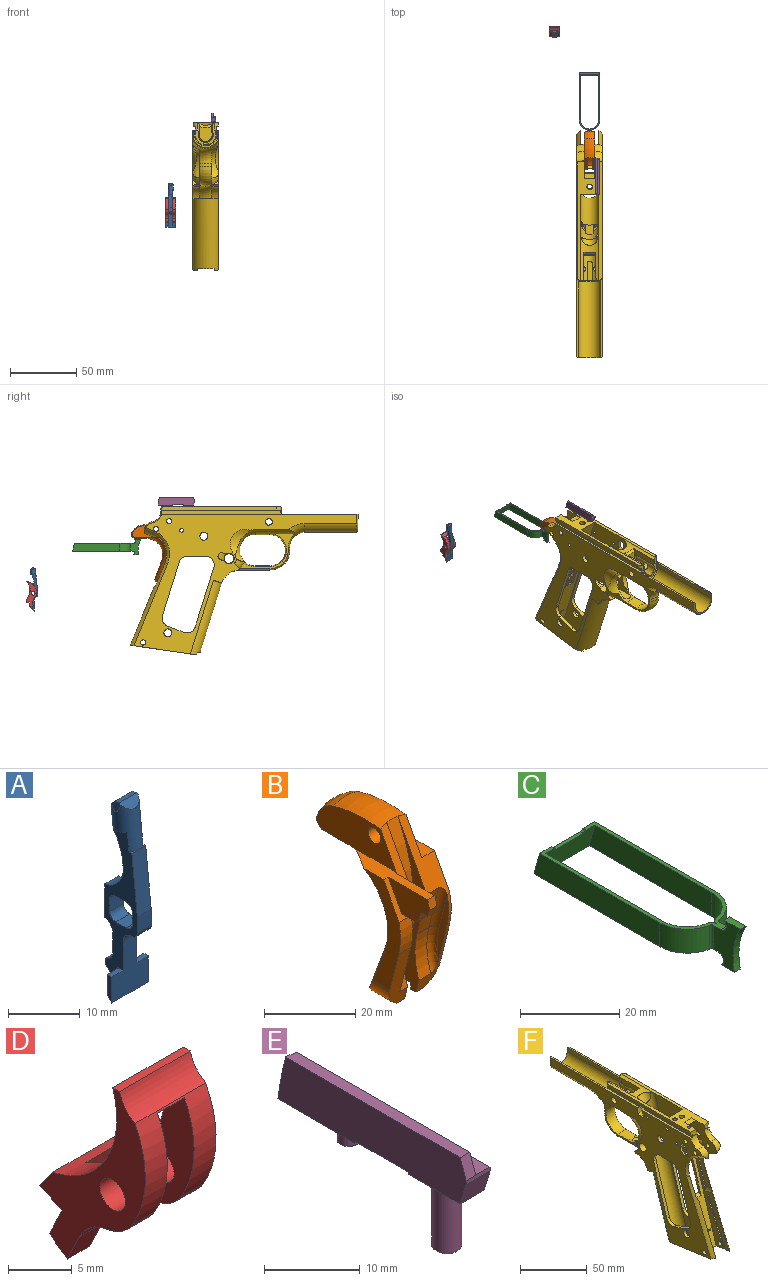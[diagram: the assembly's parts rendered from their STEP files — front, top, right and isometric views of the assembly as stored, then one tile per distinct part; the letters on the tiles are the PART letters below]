
ASSEMBLY  parts=6 mates=3
PART A: 42 faces, bbox 7.3x6.5x33 mm
  f0: cylinder r=1.97mm len=8.04mm, axis (0,0.1,0.99), area 53.4mm2, adj f2,f3,f5,f6,f7,f34,f35,f36
  f1: plane 3.38x0.76mm, normal (0,0.1,0.99), area 2.6mm2, adj f2,f3,f40,f41
  f2: plane 3.61x1.97mm, normal (0,0.77,0.64), area 7.5mm2, adj f0,f1,f40,f41
  f3: plane 3.47x1.44mm, normal (0,-0.59,0.81), area 4.8mm2, adj f0,f1,f40,f41
  f4: plane 10.31x2.72mm, normal (0,-0.99,0.1), area 28.2mm2, adj f5,f7,f15,f34,f35
  f5: plane 27.19x6.4mm, normal (-1,0,0), area 69.5mm2, adj f0,f4,f6,f8,f9,f10,f11,f12
  f6: cylinder r=9.92mm len=6.65mm, axis (-1,0,0), area 19mm2, adj f0,f5,f7,f26
  f7: plane 27.19x6.4mm, normal (1,0,0), area 69.5mm2, adj f0,f4,f6,f8,f9,f10,f11,f12
  f8: cylinder r=1.19mm len=2.72mm, axis (-1,0,0), area 5.1mm2, adj f5,f7,f9,f27
  f9: plane 2.72x2.04mm, normal (0,-1,0), area 5.5mm2, adj f5,f7,f8,f10
  f10: cylinder r=1.19mm len=2.72mm, axis (-1,0,0), area 5.1mm2, adj f5,f7,f9,f11
  f11: plane 2.72x2.04mm, normal (0,0,1), area 5.5mm2, adj f5,f7,f10,f12
  f12: cylinder r=1.19mm len=2.72mm, axis (-1,0,0), area 5.1mm2, adj f5,f7,f11,f13
  f13: plane 2.72x2.04mm, normal (0,1,0), area 5.5mm2, adj f5,f7,f12,f14
  f14: cylinder r=1.19mm len=2.72mm, axis (-1,0,0), area 5.1mm2, adj f5,f7,f13,f27
  f15: plane 2.72x2.65mm, normal (0,-1,0), area 7.2mm2, adj f4,f5,f7,f16
  f16: cylinder r=1.19mm len=2.72mm, axis (-1,0,0), area 5.1mm2, adj f5,f7,f15,f17
  f17: plane 2.72x0.02mm, normal (0,0,-1), area 0mm2, adj f5,f7,f16,f18
  f18: cylinder r=1.59mm len=2.72mm, axis (-1,0,0), area 6.8mm2, adj f5,f7,f17,f19
  f19: plane 9.44x7.24mm, normal (0,-1,0), area 45.5mm2, adj f5,f7,f18,f20,f29,f31,f32,f33
  f20: plane 7.3x3.95mm, normal (0,0.74,-0.67), area 20.3mm2, adj f5,f7,f19,f21,f28,f30,f32,f33
  f21: plane 2.72x0.79mm, normal (0,1,0), area 2.2mm2, adj f5,f7,f20,f22
  f22: cylinder r=1.98mm len=2.72mm, axis (-1,0,0), area 7.1mm2, adj f5,f7,f21,f23
  f23: plane 3.04x2.72mm, normal (0,1,0), area 8.3mm2, adj f5,f7,f22,f24
  f24: cylinder r=1.98mm len=2.72mm, axis (-1,0,0), area 7.4mm2, adj f5,f7,f23,f25
  f25: plane 5.74x2.72mm, normal (0,1,0), area 15.6mm2, adj f5,f7,f24,f26
  f26: cylinder r=4.37mm len=4.31mm, axis (-1,0,0), area 16.6mm2, adj f5,f6,f7,f25
  f27: plane 2.72x2.04mm, normal (0,0,-1), area 5.5mm2, adj f5,f7,f8,f14
  f28: plane 3.41x2.13mm, normal (0,1,0), area 7.3mm2, adj f20,f29,f33,f38
  f29: plane 2.26x1.02mm, normal (0,0,1), area 2mm2, adj f5,f19,f28,f33,f38
  f30: plane 3.41x2.13mm, normal (0,1,0), area 7.3mm2, adj f20,f31,f32,f39
  f31: plane 2.26x1.02mm, normal (0,0,1), area 2mm2, adj f7,f19,f30,f32,f39
  f32: plane 4.39x0.89mm, normal (1,0,0), area 3.5mm2, adj f19,f20,f30,f31
  f33: plane 4.39x0.89mm, normal (-1,0,0), area 3.5mm2, adj f19,f20,f28,f29
  f34: plane 1.36x0.54mm, normal (0,0.1,0.99), area 0.2mm2, adj f0,f4,f7
  f35: plane 1.36x0.54mm, normal (0,0.1,0.99), area 0.2mm2, adj f0,f4,f5
  f36: plane 2.83x0.61mm, normal (0,-0.1,-0.99), area 1.2mm2, adj f0,f7
  f37: plane 2.83x0.61mm, normal (0,-0.1,-0.99), area 1.2mm2, adj f0,f5
  f38: cylinder r=0.13mm len=3.41mm, axis (0,0,-1), area 0.7mm2, adj f5,f20,f28,f29
  f39: cylinder r=0.13mm len=3.41mm, axis (0,0,1), area 0.7mm2, adj f7,f20,f30,f31
  f40: plane 1.67x1.65mm, normal (-0.98,0.02,0.17), area 1.9mm2, adj f0,f1,f2,f3
  f41: plane 1.67x1.65mm, normal (0.98,0.02,0.17), area 1.9mm2, adj f0,f1,f2,f3
PART B: 46 faces, bbox 16.9x38.1x47.9 mm
  f0: plane 18.69x9.94mm, normal (0,-0.88,0.47), area 60.9mm2, adj f2,f3,f9,f13,f15,f17,f20,f32
  f1: plane 17.05x6.12mm, normal (0,-0.97,-0.24), area 68.5mm2, adj f2,f3,f5,f9,f37,f41,f43
  f2: cylinder r=19.05mm len=8.65mm, axis (-1,0,0), area 33mm2, adj f0,f1,f9,f43
  f3: plane 44.48x8.86mm, normal (1,0,0), area 92.1mm2, adj f0,f1,f5,f6,f7,f13,f35,f41
  f4: plane 44.47x8.86mm, normal (-1,0,0), area 92.1mm2, adj f6,f10,f13,f14,f27,f28,f35,f38
  f5: plane 2.42x1.64mm, normal (0,-0.06,-1), area 3.7mm2, adj f1,f3,f7,f37
  f6: plane 12.62x5.63mm, normal (0,-0.06,-1), area 51.1mm2, adj f3,f4,f7,f12,f28,f35,f36,f37
  f7: plane 4.57x1.82mm, normal (0,1,-0.06), area 6.4mm2, adj f3,f5,f6,f37
  f8: plane 28.65x11.28mm, normal (1,0,0), area 121mm2, adj f10,f11,f14,f21,f26,f30,f36
  f9: plane 28.65x11.28mm, normal (-1,0,0), area 121mm2, adj f0,f1,f2,f11,f17,f30,f37
  f10: plane 17.05x6.1mm, normal (0,-0.97,-0.24), area 28mm2, adj f4,f8,f26,f27,f36,f39,f40,f44
  f11: cylinder r=11.91mm len=15.72mm, axis (0,0.34,-0.94), area 252.7mm2, adj f8,f9,f12,f30,f36,f37
  f12: extruded ~14.05x3.13mm, area 20.3mm2, adj f6,f11,f36,f37
  f13: torus R=23.81mm, axis (-1,0,0), area 117.5mm2, adj f0,f3,f4,f14,f15,f16,f34,f35
  f14: plane 18.69x9.94mm, normal (0,-0.88,0.47), area 73.8mm2, adj f4,f8,f13,f16,f21,f26,f38,f45
  f15: plane 24.62x9.44mm, normal (-1,0,0), area 173.6mm2, adj f0,f13,f17,f25,f29,f30,f31,f34
  f16: plane 24.62x9.44mm, normal (1,0,0), area 173.6mm2, adj f13,f14,f21,f25,f29,f30,f31,f34
  f17: plane 25.36x3.94mm, normal (0,0,1), area 63.6mm2, adj f0,f9,f15,f18,f30,f32,f33
  f18: plane 2.57x2.21mm, normal (0,-0.98,0.21), area 5.8mm2, adj f17,f19,f32,f33
  f19: plane 2.21x1.82mm, normal (0,-0.95,-0.31), area 4.2mm2, adj f18,f24,f32,f33
  f20: plane 3.84x2.21mm, normal (0,0,-1), area 8.5mm2, adj f0,f23,f32,f33
  f21: plane 13.16x3.94mm, normal (0,0,1), area 36.6mm2, adj f8,f14,f16,f30
  f22: plane 2.26x2.21mm, normal (0,-0.95,-0.31), area 5.2mm2, adj f23,f24,f32,f33
  f23: cylinder r=1.59mm len=2.21mm, axis (-1,0,0), area 4.4mm2, adj f20,f22,f32,f33
  f24: plane 2.21x1.98mm, normal (0,0,-1), area 4.4mm2, adj f19,f22,f32,f33
  f25: cylinder r=11.91mm len=8.18mm, axis (0,-1,0), area 65.4mm2, adj f15,f16,f30,f31
  f26: cylinder r=19.05mm len=8.65mm, axis (-1,0,0), area 7.1mm2, adj f8,f10,f14,f40,f45
  f27: plane 2.39x1.64mm, normal (0,-0.06,-1), area 3.7mm2, adj f4,f10,f28,f36
  f28: plane 4.54x1.82mm, normal (0,1,-0.06), area 6.4mm2, adj f4,f6,f27,f36
  f29: cylinder r=1.98mm len=7.85mm, axis (-1,0,0), area 97.7mm2, adj f15,f16
  f30: torus R=24.61mm, axis (1,0,0), area 403.8mm2, adj f8,f9,f11,f15,f16,f17,f21,f25
  f31: revolved ~7.85x3.38mm, area 36.6mm2, adj f15,f16,f25,f34
  f32: plane 12.77x7.75mm, normal (1,0,0), area 71mm2, adj f0,f17,f18,f19,f20,f22,f23,f24
  f33: plane 12.77x7.75mm, normal (-1,0,0), area 71mm2, adj f0,f17,f18,f19,f20,f22,f23,f24
  f34: revolved ~7.85x6.03mm, area 65.7mm2, adj f13,f15,f16,f31
  f35: cylinder r=51.07mm len=42.99mm, axis (1,0,0), area 155.4mm2, adj f3,f4,f6,f13
  f36: cylinder r=6.75mm len=7.07mm, axis (0,1,0), area 32.8mm2, adj f6,f8,f10,f11,f12,f27,f28
  f37: cylinder r=6.75mm len=7.07mm, axis (0,1,0), area 32.8mm2, adj f1,f5,f6,f7,f9,f11,f12
  f38: plane 12.16x3.7mm, normal (0,-0.97,-0.24), area 46.3mm2, adj f4,f14,f39,f45
  f39: cylinder r=20.64mm len=12.01mm, axis (-1,0,0), area 45.1mm2, adj f4,f10,f38,f44
  f40: plane 18.96x3.57mm, normal (-1,0,0), area 26.1mm2, adj f10,f26,f44,f45
  f41: cylinder r=20.64mm len=12.01mm, axis (-1,0,0), area 28.5mm2, adj f1,f3,f42,f43
  f42: plane 12.16x3.03mm, normal (0,-0.97,-0.24), area 29.3mm2, adj f0,f3,f41,f43
  f43: plane 24.18x5.16mm, normal (1,0,0), area 61.2mm2, adj f0,f1,f2,f41,f42
  f44: torus R=19.05mm, axis (1,0,0), area 27.3mm2, adj f10,f39,f40,f45
  f45: cylinder r=1.59mm len=12.55mm, axis (0,-0.24,0.97), area 29.7mm2, adj f14,f26,f38,f40,f44
PART C: 26 faces, bbox 15.7x51.8x11.4 mm
  f0: plane 44.64x15.7mm, normal (0,0,1), area 85mm2, adj f2,f3,f4,f5,f6,f7,f8,f9
  f1: plane 45.47x15.7mm, normal (0,0,-1), area 94.3mm2, adj f2,f3,f4,f5,f6,f7,f8,f9
  f2: plane 35.87x5.89mm, normal (-1,0,0), area 206.6mm2, adj f0,f1,f8,f16
  f3: plane 35x5.89mm, normal (-1,0,0), area 201.5mm2, adj f0,f1,f7,f17
  f4: cylinder r=1.47mm len=5.89mm, axis (0,0,-1), area 12.1mm2, adj f0,f1,f5,f15
  f5: cylinder r=7.01mm len=6.9mm, axis (0,0,-1), area 57.7mm2, adj f0,f1,f4,f6
  f6: plane 35x5.89mm, normal (1,0,0), area 201.5mm2, adj f0,f1,f5,f17
  f7: cylinder r=7.01mm len=6.9mm, axis (0,0,-1), area 57.7mm2, adj f0,f1,f3,f15
  f8: cylinder r=7.85mm len=7.73mm, axis (0,0,-1), area 64.6mm2, adj f0,f1,f2,f9
  f9: cylinder r=0.64mm len=5.89mm, axis (0,0,-1), area 5.2mm2, adj f0,f1,f8,f10
  f10: plane 11.43x7.53mm, normal (-1,0,0), area 52.4mm2, adj f0,f1,f9,f21,f22,f23,f24,f25
  f11: plane 11.43x7.53mm, normal (1,0,0), area 52.4mm2, adj f0,f1,f12,f21,f22,f23,f24,f25
  f12: cylinder r=0.64mm len=5.89mm, axis (0,0,-1), area 5.2mm2, adj f0,f1,f11,f13
  f13: cylinder r=7.85mm len=7.73mm, axis (0,0,-1), area 64.6mm2, adj f0,f1,f12,f14
  f14: plane 35.87x5.89mm, normal (1,0,0), area 206.6mm2, adj f0,f1,f13,f16
  f15: cylinder r=1.47mm len=5.89mm, axis (0,0,-1), area 12.1mm2, adj f0,f1,f4,f7
  f16: plane 15.7x5.89mm, normal (0,0.96,0.26), area 90.9mm2, adj f0,f1,f2,f14,f18,f19,f20
  f17: plane 14.02x5.89mm, normal (0,-0.96,-0.26), area 80.7mm2, adj f0,f1,f3,f6,f18,f19,f20
  f18: cylinder r=0.64mm len=1.02mm, axis (0,1,0), area 0.8mm2, adj f0,f16,f17,f19
  f19: plane 7.78x0.87mm, normal (0,0,1), area 6.8mm2, adj f16,f17,f18,f20
  f20: cylinder r=0.64mm len=1.02mm, axis (0,1,0), area 0.8mm2, adj f0,f16,f17,f19
  f21: cylinder r=16mm len=11.43mm, axis (1,0,0), area 19.8mm2, adj f10,f11,f23,f25
  f22: cylinder r=1.52mm len=2.77mm, axis (1,0,0), area 6.5mm2, adj f1,f10,f11,f23
  f23: plane 3.77x1.68mm, normal (0,0,-1), area 6.3mm2, adj f10,f11,f21,f22
  f24: cylinder r=1.52mm len=2.77mm, axis (1,0,0), area 6.5mm2, adj f0,f10,f11,f25
  f25: plane 4.62x1.68mm, normal (0,0,1), area 7.7mm2, adj f10,f11,f21,f24
PART D: 25 faces, bbox 7.8x11.7x19 mm
  f0: cylinder r=10.01mm len=9.82mm, axis (-1,0,0), area 50.7mm2, adj f1,f7,f17,f18,f19,f22,f23,f24
  f1: cylinder r=3.96mm len=2.85mm, axis (-1,0,0), area 8.6mm2, adj f0,f2,f19,f24
  f2: cylinder r=3.96mm len=3.02mm, axis (-1,0,0), area 9.5mm2, adj f1,f3,f19,f24
  f3: plane 2.83x2.44mm, normal (0,-0.9,-0.43), area 7.6mm2, adj f2,f4,f19,f24
  f4: cylinder r=10.03mm len=2.44mm, axis (-1,0,0), area 6.1mm2, adj f3,f5,f19,f24
  f5: plane 2.87x2.44mm, normal (0,0.9,0.43), area 7.8mm2, adj f4,f12,f19,f24
  f6: cylinder r=1.41mm len=2.82mm, axis (-1,0,0), area 21.6mm2, adj f19,f24
  f7: cylinder r=3.96mm len=2.85mm, axis (-1,0,0), area 8.6mm2, adj f0,f8,f18,f23
  f8: cylinder r=3.96mm len=3.02mm, axis (-1,0,0), area 9.5mm2, adj f7,f9,f18,f23
  f9: plane 2.83x2.44mm, normal (0,-0.9,-0.43), area 7.6mm2, adj f8,f10,f18,f23
  f10: cylinder r=10.03mm len=2.44mm, axis (-1,0,0), area 6.1mm2, adj f9,f11,f18,f23
  f11: plane 2.87x2.44mm, normal (0,0.9,0.43), area 7.8mm2, adj f10,f12,f18,f23
  f12: plane 7.85x2.45mm, normal (0,0.43,-0.9), area 19.4mm2, adj f5,f11,f13,f18,f19,f20,f23,f24
  f13: plane 7.85x1.99mm, normal (0,0.81,0.58), area 19.2mm2, adj f12,f14,f18,f19
  f14: cylinder r=8.79mm len=11.43mm, axis (-1,0,0), area 87.1mm2, adj f13,f15,f18,f19,f21,f22,f23,f24
  f15: plane 7.85x0.76mm, normal (0,0,1), area 6mm2, adj f14,f17,f18,f19
  f16: cylinder r=1.41mm len=2.82mm, axis (-1,0,0), area 21.6mm2, adj f18,f23
  f17: cylinder r=3.56mm len=7.85mm, axis (-1,0,0), area 22.5mm2, adj f0,f15,f18,f19
  f18: plane 18.96x11.69mm, normal (1,0,0), area 72.8mm2, adj f0,f7,f8,f9,f10,f11,f12,f13
  f19: plane 18.96x11.69mm, normal (-1,0,0), area 72.8mm2, adj f0,f1,f2,f3,f4,f5,f6,f12
  f20: plane 2.97x0.47mm, normal (0,-0.81,-0.58), area 1.7mm2, adj f12,f21,f23,f24
  f21: cylinder r=13.1mm len=2.97mm, axis (-1,0,0), area 8.3mm2, adj f14,f20,f23,f24
  f22: cylinder r=13.1mm len=2.97mm, axis (-1,0,0), area 7mm2, adj f0,f14,f23,f24
  f23: plane 16.58x10.62mm, normal (-1,0,0), area 64.5mm2, adj f0,f7,f8,f9,f10,f11,f12,f14
  f24: plane 16.58x10.62mm, normal (1,0,0), area 64.5mm2, adj f0,f1,f2,f3,f4,f5,f6,f12
PART E: 20 faces, bbox 3.5x27.8x14.1 mm
  f0: plane 27.36x3.43mm, normal (1,0,0), area 89.6mm2, adj f2,f4,f5,f6,f7,f8,f9,f10
  f1: plane 2.49x1.42mm, normal (0,-0.94,0.34), area 3.8mm2, adj f3,f4,f11,f16
  f2: revolved ~5.94x3.51mm, area 15.9mm2, adj f0,f3,f10,f11,f16,f17
  f3: plane 25.77x1.42mm, normal (0,0,1), area 36.5mm2, adj f1,f2,f11,f16
  f4: plane 3.51x0.51mm, normal (0,-1,0), area 1.8mm2, adj f0,f1,f5,f11,f17
  f5: plane 3.51x2.92mm, normal (0,-0.95,-0.3), area 10.7mm2, adj f0,f4,f6,f11
  f6: plane 7.62x3.51mm, normal (0,0,-1), area 18.9mm2, adj f0,f5,f7,f11,f12
  f7: plane 3.51x0.25mm, normal (0,1,0), area 0.9mm2, adj f0,f6,f8,f11
  f8: plane 7.92x3.51mm, normal (0,0,-1), area 27.8mm2, adj f0,f7,f9,f11
  f9: plane 3.51x0.25mm, normal (0,-1,0), area 0.9mm2, adj f0,f8,f10,f11
  f10: plane 11.33x3.51mm, normal (0,0,-1), area 34.3mm2, adj f0,f2,f9,f11,f14
  f11: plane 27.79x5.92mm, normal (-1,0,0), area 157.1mm2, adj f1,f2,f3,f4,f5,f6,f7,f8
  f12: cylinder r=1.58mm len=7.87mm, axis (0,0,1), area 78.2mm2, adj f6,f19
  f13: plane 2.65x2.65mm, normal (0,0,-1), area 5.5mm2, adj f19
  f14: cylinder r=1.23mm len=2.45mm, axis (0,0,1), area 15.6mm2, adj f10,f18
  f15: plane 1.94x1.94mm, normal (0,0,-1), area 3mm2, adj f18
  f16: plane 27.06x2.49mm, normal (1,0,0), area 65.6mm2, adj f1,f2,f3,f17
  f17: plane 27.06x2.08mm, normal (0,0,1), area 56.1mm2, adj f0,f2,f4,f16
  f18: cone r=0.97mm half-angle=45deg, axis (0,0,1), area 2.5mm2, adj f14,f15
  f19: cone r=1.33mm half-angle=45deg, axis (0,0,1), area 3.3mm2, adj f12,f13
PART F: 210 faces, bbox 73.5x173.8x115.4 mm
  f0: plane 33.29x27.82mm, normal (-1,0,0), area 401.2mm2, adj f3,f13,f22,f25,f34,f81,f95,f96
  f1: plane 33.29x27.82mm, normal (1,0,0), area 393.4mm2, adj f2,f4,f13,f23,f24,f33,f71,f95
  f2: plane 10.06x4.05mm, normal (0,-0.97,0.25), area 12.9mm2, adj f1,f4,f165,f167,f200,f201
  f3: plane 10.06x4.05mm, normal (0,-0.97,0.25), area 12.9mm2, adj f0,f169,f172,f175,f202,f203
  f4: plane 18.49x4.01mm, normal (0,0,-1), area 24.4mm2, adj f1,f2,f97,f167,f181,f191,f199,f200
  f5: plane 20.01x4.01mm, normal (0,0,1), area 25.8mm2, adj f6,f7,f10,f21,f167,f177,f192,f197
  f6: plane 73.12x22.78mm, normal (0,-0.95,0.3), area 781.7mm2, adj f5,f12,f14,f16,f176,f177,f178,f179
  f7: plane 73.41x22.87mm, normal (0,0.95,-0.3), area 819.6mm2, adj f5,f10,f11,f12,f14,f16,f178,f179
  f8: cylinder r=7mm len=6.95mm, axis (0,-0.3,-0.95), area 9mm2, adj f11,f114,f131,f132,f133,f184
  f9: cylinder r=7mm len=81.01mm, axis (0,-0.3,-0.95), area 1625.7mm2, adj f10,f11,f16,f45,f47,f114,f130,f131
  f10: plane 77.48x52.15mm, normal (1,0,0), area 706.4mm2, adj f5,f7,f9,f16,f72,f73,f74,f75
  f11: plane 77.48x52.15mm, normal (-1,0,0), area 705.6mm2, adj f7,f8,f9,f12,f16,f61,f62,f63
  f12: plane 20.01x4.01mm, normal (0,0,1), area 25.8mm2, adj f6,f7,f11,f170,f172,f176,f186,f198
  f13: plane 90.81x19.17mm, normal (0,0,1), area 681.4mm2, adj f0,f1,f35,f56,f83,f84,f86,f97
  f14: cylinder r=6.73mm len=2.34mm, axis (0,-0.25,-0.97), area 3.1mm2, adj f6,f7,f179,f180
  f15: cylinder r=11.91mm len=63.81mm, axis (0,-0.38,-0.93), area 242.5mm2, adj f16,f23,f38,f167,f168,f177
  f16: plane 50.11x19.42mm, normal (0,-0.14,-0.99), area 283.6mm2, adj f6,f7,f9,f10,f11,f15,f18,f19
  f17: cylinder r=1.99mm len=3.99mm, axis (-1,0,0), area 35mm2, adj f38,f177
  f18: plane 40.77x17.31mm, normal (0,-0.92,0.39), area 46.5mm2, adj f16,f20,f94,f177
  f19: plane 41.27x17.52mm, normal (0,0.92,-0.39), area 47.1mm2, adj f16,f20,f94,f177
  f20: cylinder r=6.75mm len=4.17mm, axis (0,-0.92,0.39), area 8mm2, adj f18,f19,f94,f177
  f21: plane 28.77x7.41mm, normal (0,-0.97,0.25), area 30.4mm2, adj f5,f167,f168,f177
  f22: torus R=25.99mm, axis (1,0,0), area 89.3mm2, adj f0,f26,f34,f42,f172,f173
  f23: torus R=25.99mm, axis (1,0,0), area 89.3mm2, adj f1,f15,f33,f38,f167,f174
  f24: plane 8.26x4.01mm, normal (0,0.97,-0.25), area 26.5mm2, adj f1,f166,f167,f174
  f25: plane 8.26x4.01mm, normal (0,0.97,-0.25), area 26.5mm2, adj f0,f169,f172,f173
  f26: cylinder r=11.91mm len=63.81mm, axis (0,-0.38,-0.93), area 242.5mm2, adj f16,f22,f42,f171,f172,f176
  f27: cylinder r=7mm len=30.29mm, axis (0,-0.3,-0.95), area 449.3mm2, adj f46,f47,f56,f97,f98,f108,f109,f110
  f28: cylinder r=10.32mm len=57.76mm, axis (0,-0.3,-0.95), area 1423.3mm2, adj f16,f38,f42,f146,f162,f163,f164
  f29: plane 149.05x3.32mm, normal (0,0,1), area 231.2mm2, adj f31,f42,f49,f50,f113,f118,f127,f161
  f30: plane 51.23x1.7mm, normal (0,0,1), area 86.9mm2, adj f32,f38,f107,f160
  f31: plane 90.31x3.02mm, normal (1,0,0), area 272.4mm2, adj f29,f59,f113,f157,f161
  f32: plane 90.31x3.02mm, normal (-1,0,0), area 258.8mm2, adj f30,f57,f60,f107,f109,f112,f156,f160
  f33: cylinder r=11.91mm len=7.67mm, axis (0,0.92,-0.38), area 45.3mm2, adj f1,f23,f38,f159
  f34: cylinder r=11.91mm len=7.67mm, axis (0,0.92,-0.38), area 45.3mm2, adj f0,f22,f42,f158
  f35: plane 87.01x2.54mm, normal (-1,0,0), area 220.8mm2, adj f13,f60,f112,f156
  f36: torus R=2.06mm, axis (-1,0,0), area 38mm2, adj f37,f38,f41,f155
  f37: torus R=25.23mm, axis (-1,0,0), area 401.4mm2, adj f36,f38,f40,f41,f42,f45,f46,f47
  f38: plane 168.77x105.92mm, normal (-1,0,0), area 4040.2mm2, adj f15,f16,f17,f23,f28,f30,f33,f36
  f39: cylinder r=14.29mm len=12.31mm, axis (1,0,0), area 83.2mm2, adj f42,f146,f148,f153
  f40: plane 42.11x26.44mm, normal (1,0,0), area 137.6mm2, adj f37,f44,f48,f139,f141,f142,f143,f144
  f41: plane 42.11x26.44mm, normal (-1,0,0), area 137.6mm2, adj f36,f37,f44,f48,f139,f141,f142,f143
  f42: plane 168.76x105.92mm, normal (1,0,0), area 4107.5mm2, adj f16,f22,f26,f28,f29,f34,f37,f39
  f43: cylinder r=14.29mm len=12.31mm, axis (1,0,0), area 83.2mm2, adj f38,f146,f147,f154
  f44: torus R=25.23mm, axis (1,0,0), area 359.2mm2, adj f40,f41,f142,f143
  f45: plane 22.72x6.83mm, normal (0,0,1), area 133.7mm2, adj f9,f37,f47,f114
  f46: plane 15.49x6.83mm, normal (0,0,-1), area 87.8mm2, adj f27,f37,f47,f114
  f47: plane 23.22x20.5mm, normal (1,0,0), area 172.7mm2, adj f9,f27,f37,f45,f46,f130,f189,f190
  f48: torus R=21.43mm, axis (-1,0,0), area 324.1mm2, adj f38,f40,f41,f42,f140,f143,f144
  f49: plane 17.77x13.13mm, normal (0,1,0), area 33.5mm2, adj f29,f57,f116,f117,f118,f207,f208,f209
  f50: plane 16.15x5.65mm, normal (0,1,0), area 30.9mm2, adj f29,f53,f56,f113,f120,f121,f126,f127
  f51: plane 3.03x0.15mm, normal (0,1,0), area 0.3mm2, adj f124,f126
  f52: plane 16.15x5.65mm, normal (0,1,0), area 30.9mm2, adj f53,f56,f57,f112,f119,f122,f125,f126
  f53: cylinder r=5.7mm len=19.35mm, axis (0,1,0), area 376.6mm2, adj f50,f52,f54,f55,f58,f80,f119,f120
  f54: plane 19.06x6.86mm, normal (1,0,0), area 81.4mm2, adj f53,f56,f115,f119,f128,f129
  f55: plane 19.06x6.86mm, normal (-1,0,0), area 81.4mm2, adj f53,f56,f115,f120,f128,f129
  f56: cylinder r=13.5mm len=35.75mm, axis (0,1,0), area 221.1mm2, adj f13,f27,f50,f52,f54,f55,f111,f112
  f57: plane 91.8x3.31mm, normal (0,0,1), area 134.1mm2, adj f32,f38,f49,f52,f109,f112,f117,f125
  f58: cylinder r=2.55mm len=6.62mm, axis (-1,0,0), area 77.8mm2, adj f42,f53
  f59: plane 90.01x1.56mm, normal (0,0,-1), area 139.2mm2, adj f31,f83,f113,f157
  f60: plane 90.01x1.56mm, normal (0,0,-1), area 139.2mm2, adj f32,f35,f112,f156
  f61: plane 45.24x14.09mm, normal (0,-0.95,0.3), area 127mm2, adj f11,f42,f62,f68
  f62: cylinder r=6.35mm len=8.3mm, axis (-1,0,0), area 27.7mm2, adj f11,f42,f61,f63
  f63: plane 12.65x4.76mm, normal (0,0.35,0.94), area 36.2mm2, adj f11,f42,f62,f64
  f64: cylinder r=6.35mm len=7.83mm, axis (-1,0,0), area 25.7mm2, adj f11,f42,f63,f65
  f65: plane 40.48x12.61mm, normal (0,0.95,-0.3), area 113.6mm2, adj f11,f42,f64,f66
  f66: cylinder r=6.35mm len=6.06mm, axis (-1,0,0), area 21.6mm2, adj f11,f42,f65,f67
  f67: plane 14.13x2.68mm, normal (0,0,-1), area 37.9mm2, adj f11,f42,f66,f68
  f68: cylinder r=6.35mm len=8.24mm, axis (-1,0,0), area 31.9mm2, adj f11,f42,f61,f67
  f69: cylinder r=3mm len=5.99mm, axis (-1,0,0), area 50.5mm2, adj f11,f42
  f70: cylinder r=3mm len=5.99mm, axis (-1,0,0), area 50.5mm2, adj f42,f98
  f71: cylinder r=1.98mm len=5.74mm, axis (-1,0,0), area 71.4mm2, adj f1,f38
  f72: plane 45.24x14.09mm, normal (0,-0.95,0.3), area 127mm2, adj f10,f38,f73,f79
  f73: cylinder r=6.35mm len=8.3mm, axis (-1,0,0), area 27.7mm2, adj f10,f38,f72,f74
  f74: plane 12.65x4.76mm, normal (0,0.35,0.94), area 36.2mm2, adj f10,f38,f73,f75
  f75: cylinder r=6.35mm len=7.83mm, axis (-1,0,0), area 25.7mm2, adj f10,f38,f74,f76
  f76: plane 40.48x12.61mm, normal (0,0.95,-0.3), area 113.6mm2, adj f10,f38,f75,f77
  f77: cylinder r=6.35mm len=6.06mm, axis (-1,0,0), area 21.6mm2, adj f10,f38,f76,f78
  f78: plane 14.13x2.68mm, normal (0,0,-1), area 37.9mm2, adj f10,f38,f77,f79
  f79: cylinder r=6.35mm len=8.24mm, axis (-1,0,0), area 31.9mm2, adj f10,f38,f72,f78
  f80: cylinder r=2.55mm len=6.62mm, axis (-1,0,0), area 77.9mm2, adj f38,f53
  f81: cylinder r=1.98mm len=5.74mm, axis (-1,0,0), area 71.4mm2, adj f0,f42
  f82: cylinder r=1.99mm len=3.99mm, axis (-1,0,0), area 35mm2, adj f42,f176
  f83: plane 87.01x2.54mm, normal (1,0,0), area 220.8mm2, adj f13,f59,f113,f157
  f84: cylinder r=1.58mm len=8.38mm, axis (0,0,1), area 83.3mm2, adj f13,f85
  f85: plane 3.16x3.16mm, normal (0,0,1), area 7.9mm2, adj f84
  f86: cylinder r=1.23mm len=3.18mm, axis (0,0,1), area 24.4mm2, adj f13,f87
  f87: plane 2.45x2.45mm, normal (0,0,1), area 4.7mm2, adj f86
  f88: cylinder r=3mm len=5.99mm, axis (-1,0,0), area 50.5mm2, adj f10,f38
  f89: cylinder r=3mm len=5.99mm, axis (-1,0,0), area 50.5mm2, adj f38,f97
  f90: plane 40.77x17.31mm, normal (0,-0.92,0.39), area 46.5mm2, adj f16,f91,f93,f176
  f91: cylinder r=6.75mm len=4.17mm, axis (0,-0.92,0.39), area 8mm2, adj f90,f92,f93,f176
  f92: plane 41.27x17.52mm, normal (0,0.92,-0.39), area 47.1mm2, adj f16,f91,f93,f176
  f93: plane 38.21x17.98mm, normal (-1,0,0), area 84.2mm2, adj f16,f90,f91,f92
  f94: plane 38.21x17.98mm, normal (1,0,0), area 84.2mm2, adj f16,f18,f19,f20
  f95: cylinder r=73.25mm len=7.87mm, axis (1,0,0), area 8mm2, adj f0,f1,f96,f135
  f96: cylinder r=38.1mm len=14.72mm, axis (1,0,0), area 108.5mm2, adj f0,f1,f95,f136,f181
  f97: plane 38.07x27.81mm, normal (1,0,0), area 765.7mm2, adj f4,f13,f27,f89,f100,f101,f107,f109
  f98: plane 38.07x27.81mm, normal (-1,0,0), area 787.6mm2, adj f13,f27,f70,f175,f181,f185,f187
  f99: cylinder r=2mm len=5.74mm, axis (1,0,0), area 72.1mm2, adj f1,f38
  f100: cylinder r=1.19mm len=2.68mm, axis (-1,0,0), area 20mm2, adj f38,f97
  f101: cylinder r=1.19mm len=2.68mm, axis (-1,0,0), area 20mm2, adj f38,f97
  f102: cylinder r=1.4mm len=5.74mm, axis (-1,0,0), area 50.4mm2, adj f1,f38
  f103: cylinder r=2.67mm len=5.74mm, axis (-1,0,0), area 48.8mm2, adj f1,f38,f104,f106,f165,f166
  f104: cylinder r=3.2mm len=5.23mm, axis (-1,0,0), area 19.8mm2, adj f38,f103,f105,f165
  f105: cylinder r=2.67mm len=4.76mm, axis (-1,0,0), area 12.9mm2, adj f38,f104,f106,f165,f166,f167
  f106: plane 5.01x4.73mm, normal (0,0.95,-0.31), area 14.5mm2, adj f38,f103,f105,f166
  f107: plane 5.96x2.68mm, normal (0,1,-0.07), area 15.9mm2, adj f30,f32,f38,f97,f109,f110
  f108: plane 5.82x5.25mm, normal (0,-1,0.07), area 24.3mm2, adj f27,f38,f109,f110
  f109: cylinder r=3.01mm len=6.01mm, axis (1,0,0), area 12.3mm2, adj f27,f32,f38,f57,f97,f107,f108
  f110: plane 6.19x5.12mm, normal (0,0,1), area 20mm2, adj f27,f38,f97,f107,f108
  f111: cylinder r=5.99mm len=11.86mm, axis (0,0.52,0.85), area 90mm2, adj f27,f56
  f112: cylinder r=3.17mm len=5.56mm, axis (0,0,-1), area 17.7mm2, adj f13,f32,f35,f52,f56,f57,f60
  f113: cylinder r=3.17mm len=5.56mm, axis (0,0,-1), area 17.7mm2, adj f13,f29,f31,f50,f56,f59,f83
  f114: plane 23.22x20.5mm, normal (-1,0,0), area 167.4mm2, adj f8,f9,f27,f37,f45,f46,f131,f183
  f115: plane 11.3x9.88mm, normal (0,1,0), area 93.4mm2, adj f54,f55,f128,f129
  f116: cylinder r=8.36mm len=57.54mm, axis (0,1,0), area 1510.5mm2, adj f49,f117,f118,f126
  f117: plane 57.54x3.61mm, normal (1,0,0), area 207.5mm2, adj f49,f57,f116,f125
  f118: plane 57.54x3.61mm, normal (-1,0,0), area 207.5mm2, adj f29,f49,f116,f127
  f119: plane 5.5x3.31mm, normal (0.99,0.1,0), area 16.1mm2, adj f52,f53,f54,f56
  f120: plane 5.5x3.31mm, normal (-0.99,0.1,0), area 16.1mm2, adj f50,f53,f55,f56
  f121: plane 13.14x2.08mm, normal (-1,0,0), area 27.3mm2, adj f50,f53,f123,f124,f126
  f122: plane 13.14x2.08mm, normal (1,0,0), area 27.3mm2, adj f52,f53,f123,f124,f126
  f123: cylinder r=1.94mm len=3.89mm, axis (0,0,-1), area 12.7mm2, adj f53,f121,f122,f124
  f124: plane 15.09x3.89mm, normal (0,0,1), area 57mm2, adj f51,f121,f122,f123,f126
  f125: cylinder r=0.76mm len=3.61mm, axis (0,0,1), area 4.3mm2, adj f52,f57,f117,f126
  f126: torus R=7.59mm, axis (0,1,0), area 30.3mm2, adj f50,f51,f52,f116,f121,f122,f124,f125
  f127: cylinder r=0.76mm len=3.61mm, axis (0,0,-1), area 4.3mm2, adj f29,f50,f118,f126
  f128: torus R=4.94mm, axis (0,-1,0), area 26.8mm2, adj f53,f54,f55,f115
  f129: cone r=13.5mm half-angle=45deg, axis (0,1,0), area 21.2mm2, adj f54,f55,f56,f115
  f130: cylinder r=3.64mm len=7.29mm, axis (-1,0,0), area 148.9mm2, adj f9,f38,f47
  f131: cylinder r=3.98mm len=7.95mm, axis (1,0,0), area 121.2mm2, adj f8,f9,f42,f114,f132,f134
  f132: plane 5.04x2.76mm, normal (0,-0.3,-0.95), area 11.2mm2, adj f8,f42,f131,f133
  f133: cylinder r=2.74mm len=5.36mm, axis (1,0,0), area 24.2mm2, adj f8,f9,f11,f42,f132,f134
  f134: plane 5.04x2.76mm, normal (0,0.3,0.95), area 11.2mm2, adj f9,f42,f131,f133
  f135: plane 7.88x4.03mm, normal (0,-0.09,1), area 31.8mm2, adj f0,f1,f13,f95
  f136: cylinder r=2.78mm len=11.66mm, axis (0,0.1,0.99), area 126.8mm2, adj f96,f137,f181
  f137: plane 5.56x5.53mm, normal (0,-0.1,-0.99), area 10.6mm2, adj f136,f138
  f138: cylinder r=2.08mm len=5.39mm, axis (0,0.1,0.99), area 62.3mm2, adj f13,f137
  f139: cylinder r=10.32mm len=22.81mm, axis (0,1,0), area 220.6mm2, adj f40,f41,f141,f148,f149
  f140: cylinder r=10.32mm len=39.78mm, axis (0,1,0), area 998.7mm2, adj f38,f42,f48,f209
  f141: torus R=4.67mm, axis (-1,0,0), area 222mm2, adj f40,f41,f139,f144
  f142: cylinder r=13.49mm len=10.77mm, axis (0,1,0), area 102.5mm2, adj f37,f40,f41,f44
  f143: cylinder r=13.49mm len=30.08mm, axis (0,1,0), area 435.4mm2, adj f37,f38,f40,f41,f42,f44,f48
  f144: cylinder r=10.32mm len=9.32mm, axis (0,0,-1), area 23.2mm2, adj f40,f41,f48,f141
  f145: torus R=2.06mm, axis (-1,0,0), area 38mm2, adj f37,f40,f42,f148,f152,f153
  f146: plane 19.4x6.48mm, normal (0,-0.3,-0.95), area 32.2mm2, adj f28,f38,f39,f42,f43,f147,f148,f149
  f147: plane 14.62x10.86mm, normal (1,0,0), area 20mm2, adj f43,f146,f149,f154
  f148: plane 14.62x10.86mm, normal (-1,0,0), area 20mm2, adj f39,f139,f145,f146,f149
  f149: torus R=24.61mm, axis (1,0,0), area 177.1mm2, adj f139,f146,f147,f148
  f150: sphere r=22.23mm, area 131.6mm2, adj f37,f42
  f151: sphere r=22.23mm, area 131.6mm2, adj f37,f38
  f152: plane 5.03x4.16mm, normal (0,0.68,0.74), area 10.5mm2, adj f42,f145,f153
  f153: cylinder r=11.24mm len=5.02mm, axis (-1,0,0), area 8.6mm2, adj f39,f42,f145,f152
  f154: cylinder r=11.24mm len=5.02mm, axis (-1,0,0), area 8.6mm2, adj f38,f43,f147,f155
  f155: plane 5.03x4.15mm, normal (0,0.68,0.74), area 10.5mm2, adj f36,f38,f154
  f156: extruded ~5.6x4.2mm, area 20.9mm2, adj f1,f13,f32,f35,f60,f160
  f157: extruded ~5.6x4.2mm, area 20.9mm2, adj f0,f13,f31,f59,f83,f161
  f158: revolved ~8.51x5.87mm, area 50.4mm2, adj f0,f34,f42,f161
  f159: revolved ~8.51x5.87mm, area 50.4mm2, adj f1,f33,f38,f160
  f160: torus R=58.65mm, axis (1,0,0), area 62.8mm2, adj f1,f30,f32,f38,f156,f159
  f161: torus R=58.65mm, axis (1,0,0), area 62.7mm2, adj f0,f29,f31,f42,f157,f158
  f162: plane 4.23x2.49mm, normal (-1,0,0), area 7.4mm2, adj f9,f16,f28,f164
  f163: plane 4.23x2.49mm, normal (1,0,0), area 7.4mm2, adj f9,f16,f28,f164
  f164: plane 14.27x7.26mm, normal (0,-0.14,-0.99), area 26.9mm2, adj f9,f28,f162,f163
  f165: cylinder r=7.62mm len=7.31mm, axis (0,0.97,-0.25), area 16.8mm2, adj f1,f2,f103,f104,f105,f167
  f166: cylinder r=7.62mm len=7.59mm, axis (0,0.97,-0.25), area 34.1mm2, adj f1,f24,f103,f105,f106,f167
  f167: plane 37.75x32.55mm, normal (1,0,0), area 326.6mm2, adj f2,f4,f5,f15,f21,f23,f24,f105
  f168: cylinder r=6.75mm len=8.26mm, axis (0,0.97,-0.25), area 26.6mm2, adj f15,f21,f167,f177
  f169: cylinder r=7.62mm len=13.58mm, axis (0,0.97,-0.25), area 101mm2, adj f0,f3,f25,f172
  f170: plane 28.77x7.41mm, normal (0,-0.97,0.25), area 30.4mm2, adj f12,f171,f172,f176
  f171: cylinder r=6.75mm len=8.26mm, axis (0,0.97,-0.25), area 26.6mm2, adj f26,f170,f172,f176
  f172: plane 37.75x32.55mm, normal (-1,0,0), area 331.9mm2, adj f3,f12,f22,f25,f26,f169,f170,f171
  f173: plane 5.38x4.12mm, normal (0,0,-1), area 13.7mm2, adj f0,f22,f25,f172
  f174: plane 5.37x4.11mm, normal (0,0,-1), area 13.7mm2, adj f1,f23,f24,f167
  f175: plane 18.49x4.01mm, normal (0,0,-1), area 24.4mm2, adj f0,f3,f98,f172,f181,f187,f203,f204
  f176: plane 73.12x36.36mm, normal (-1,0,0), area 507.1mm2, adj f6,f12,f16,f26,f82,f90,f91,f92
  f177: plane 73.12x36.36mm, normal (1,0,0), area 507.1mm2, adj f5,f6,f15,f16,f17,f18,f19,f20
  f178: cylinder r=6.73mm len=2.34mm, axis (0,-0.25,-0.97), area 3.1mm2, adj f6,f7,f179,f180
  f179: plane 10.85x1.92mm, normal (0,-0.25,-0.97), area 17.6mm2, adj f6,f7,f14,f178
  f180: plane 10.92x1.92mm, normal (0,0.25,0.97), area 17.8mm2, adj f6,f7,f14,f178
  f181: plane 28.28x14.46mm, normal (0,0.95,-0.3), area 310.9mm2, adj f0,f1,f4,f13,f96,f97,f98,f136
  f182: plane 21.07x6.45mm, normal (-1,0,0), area 136mm2, adj f183,f184,f185,f188
  f183: cylinder r=6.86mm len=6.6mm, axis (0,0,-1), area 57.2mm2, adj f114,f182,f184,f185
  f184: plane 28.5x5.32mm, normal (0,0,1), area 57.2mm2, adj f8,f11,f114,f182,f183,f186,f188
  f185: plane 28.5x5.32mm, normal (0,0,-1), area 49.5mm2, adj f27,f98,f114,f182,f183,f187,f188
  f186: plane 0.95x0.41mm, normal (0,1,0), area 0.4mm2, adj f11,f12,f184,f188
  f187: plane 0.95x0.13mm, normal (0,1,0), area 0.1mm2, adj f98,f175,f185,f188
  f188: cylinder r=0.69mm len=6.45mm, axis (0,0,-1), area 3.5mm2, adj f172,f182,f184,f185,f186,f187
  f189: plane 28.5x5.32mm, normal (0,0,-1), area 49.5mm2, adj f27,f47,f97,f191,f193,f194,f195
  f190: plane 28.5x5.32mm, normal (0,0,1), area 57.2mm2, adj f9,f10,f47,f192,f193,f194,f195
  f191: plane 0.95x0.13mm, normal (0,1,0), area 0.1mm2, adj f4,f97,f189,f194
  f192: plane 0.95x0.41mm, normal (0,1,0), area 0.4mm2, adj f5,f10,f190,f194
  f193: plane 21.07x6.45mm, normal (1,0,0), area 136mm2, adj f189,f190,f194,f195
  f194: cylinder r=0.69mm len=6.45mm, axis (0,0,-1), area 3.5mm2, adj f167,f189,f190,f191,f192,f193
  f195: cylinder r=6.86mm len=6.6mm, axis (0,0,-1), area 57.2mm2, adj f47,f189,f190,f193
  f196: cylinder r=38.1mm len=7.87mm, axis (1,0,0), area 22.7mm2, adj f6,f7,f197,f198
  f197: plane 31.72x11.95mm, normal (1,0,0), area 64.2mm2, adj f5,f6,f7,f196
  f198: plane 31.72x11.95mm, normal (-1,0,0), area 64.2mm2, adj f6,f7,f12,f196
  f199: plane 7.31x2.95mm, normal (0,-0.95,0.3), area 17.6mm2, adj f1,f4,f200,f201
  f200: plane 4.35x3.04mm, normal (1,0,0), area 9.5mm2, adj f2,f4,f199,f201
  f201: cylinder r=6.86mm len=6.57mm, axis (0,0.95,-0.3), area 25.6mm2, adj f1,f2,f199,f200
  f202: cylinder r=6.86mm len=6.57mm, axis (0,0.95,-0.3), area 25.6mm2, adj f0,f3,f203,f204
  f203: plane 4.35x3.04mm, normal (-1,0,0), area 9.5mm2, adj f3,f175,f202,f204
  f204: plane 7.31x2.95mm, normal (0,-0.95,0.3), area 17.6mm2, adj f0,f175,f202,f203
  f205: cylinder r=1.4mm len=5.74mm, axis (1,0,0), area 50.4mm2, adj f0,f42
  f206: cylinder r=2mm len=5.74mm, axis (1,0,0), area 72.1mm2, adj f0,f42
  f207: plane 7.19x0.8mm, normal (0.71,0.71,0), area 8mm2, adj f29,f42,f49,f209
  f208: plane 7.19x0.8mm, normal (-0.71,0.71,0), area 8mm2, adj f38,f49,f57,f209
  f209: cone r=9.53mm half-angle=45deg, axis (0,-1,0), area 26.9mm2, adj f49,f140,f207,f208
PLACE A t=(-145.35,-176.42,-61.72)mm
PLACE B rot(axis=(1,0,0),0.1deg) t=(-118.87,-268.71,0.69)mm
PLACE C t=(-118.96,-241.41,-16.27)mm
PLACE D rot(axis=(-1,0,0),30deg) t=(-145.34,-175.77,-48.12)mm
PLACE E t=(-112.89,-294.8,18.75)mm
PLACE F rot(axis=(0,0,1),180deg) t=(-118.86,-354.26,6.03)mm
MATE revolute B.f29 <-> F.f71  axis (-1,0,0) through (-122.8,-268.71,0.69)mm
MATE planar F.f12 <-> C.f1  axis (0,0,1) through (-126.81,-282.26,-16.27)mm
MATE slider E.f19 <-> F.f84  axis (0,0,1) through (-112.94,-293.53,18.75)mm
